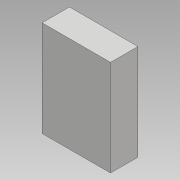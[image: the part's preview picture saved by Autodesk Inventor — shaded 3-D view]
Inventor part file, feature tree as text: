
AUTODESK INVENTOR PART (.ipt)
format: ipt  version: 2017 (Build 210142000, 142)  size: 71,168 bytes
history: native  units: mm
features: other x1, extrude x1, sketch x1
ambient origin geometry x8: Origin, YZ Plane, XZ Plane, XY Plane, X Axis, Y Axis, Z Axis, Center Point
bodies: Body1 (feature_tree)
feature tree (3):
  other  "ソリッド1"
  extrude  "押し出し1"  Depth=25.0mm
  sketch  "スケッチ1"
